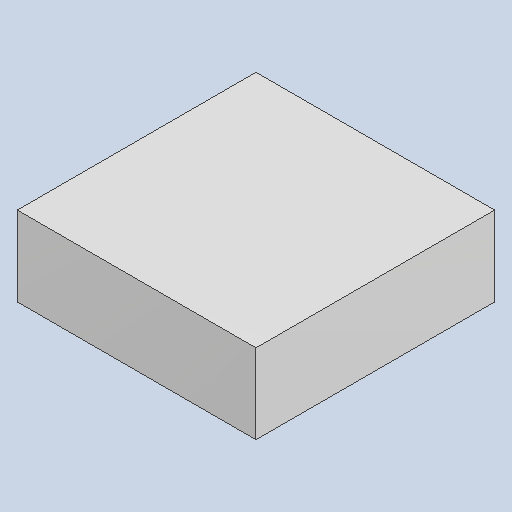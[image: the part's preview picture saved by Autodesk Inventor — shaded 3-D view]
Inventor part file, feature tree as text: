
AUTODESK INVENTOR PART (.ipt)
format: ipt  version: 2023.4 (Build 274418000, 418)  size: 79,872 bytes
history: native  units: mm
features: extrude x1
ambient origin geometry x8: Origin, YZ Plane, XZ Plane, XY Plane, X Axis, Y Axis, Z Axis, Center Point
bodies: Solid1 (feature_tree)
feature tree (1):
  extrude  "Extruded_44"  [1 undecoded]
note: 1 required parameter value undecoded (feature->parameter linkage not recoverable at this tier; creation-order binding heuristic only, values carry confidence <= 0.55)
